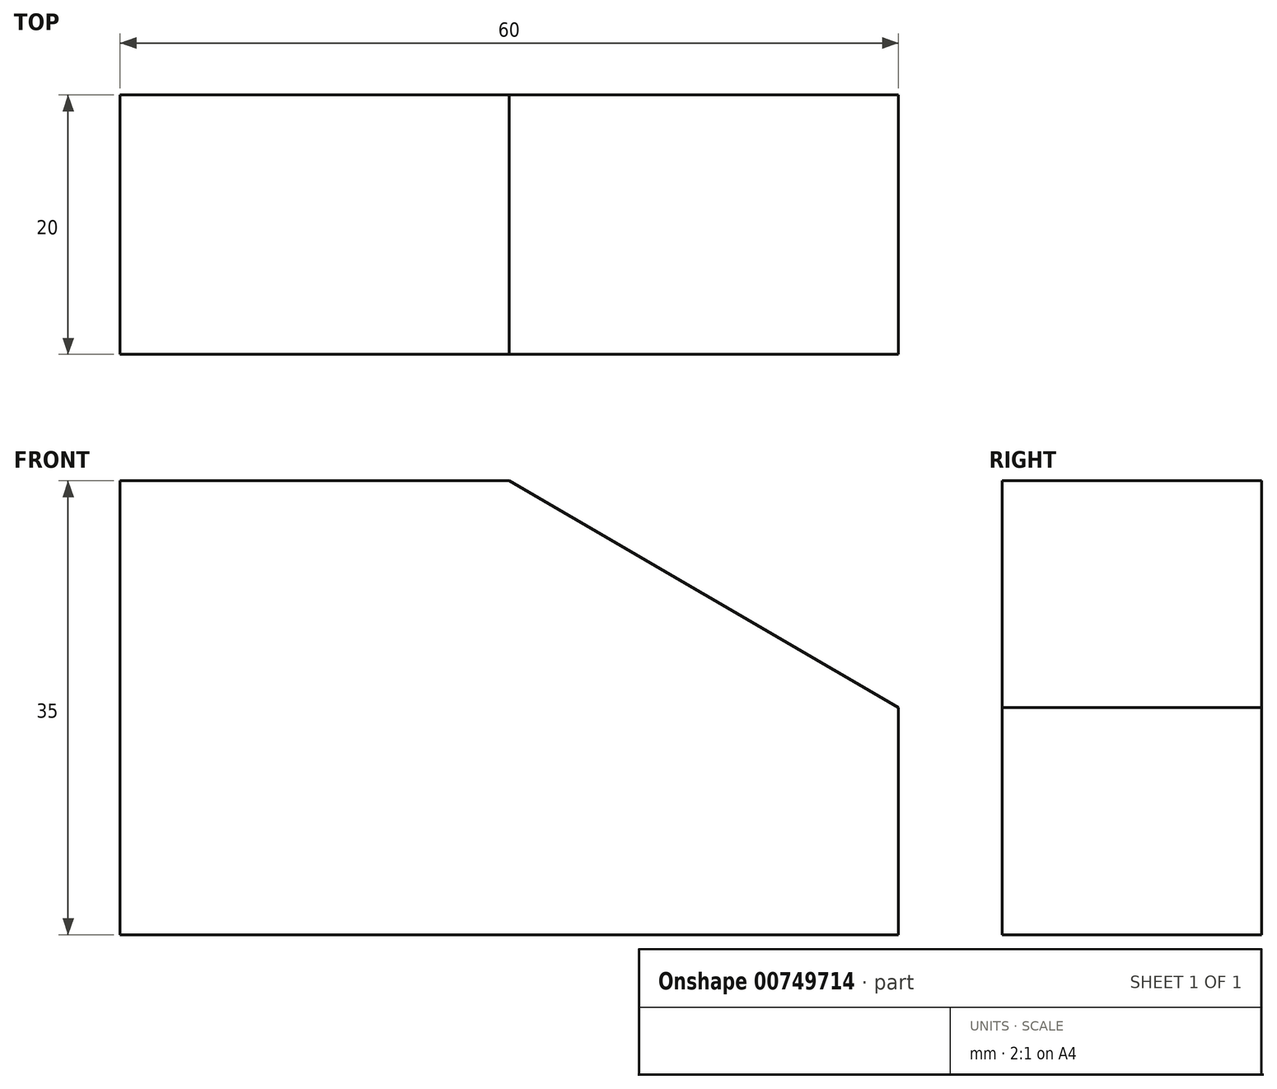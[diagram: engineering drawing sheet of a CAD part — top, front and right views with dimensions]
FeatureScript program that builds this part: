
annotation { "Feature Type Name" : "Feature", "Feature Type Description" : "" }
export const myFeature = defineFeature(function(context is Context, id is Id, definition is map)
    precondition{}
    {
        {
            var Q0;
            Q0=qCreatedBy(makeId("Front.planeOp"),FACE);
            var sketch = newSketch(context, id + "F0", { "sketchPlane" : qUnion([Q0])});
            skLineSegment(sketch, "E0.bottom", {"start": v(0, 0) * mm, "end": v(60, 0) * mm});
            skLineSegment(sketch, "E0.top", {"start": v(0, 35) * mm, "end": v(30, 35) * mm});
            skLineSegment(sketch, "E0.left", {"start": v(0, 0) * mm, "end": v(0, 35) * mm});
            skLineSegment(sketch, "E0.right", {"start": v(60, 0) * mm, "end": v(60, 17.5) * mm});
            skLineSegment(sketch, "E1", {"start": v(30, 35) * mm, "end": v(60, 17.5) * mm});
            skSolve(sketch);
        }
        {
            var Q0;
            Q0 = qSketchRegion(id + "F0", true);
            extrude(context, id + "F1", {"entities" : qUnion([Q0]), "depth" : 20 * mm, "offsetDistance" : 25 * mm});
        }
    });
